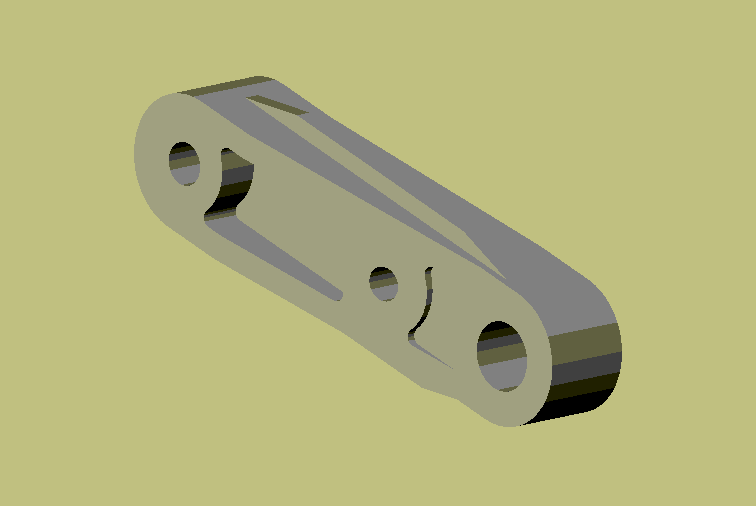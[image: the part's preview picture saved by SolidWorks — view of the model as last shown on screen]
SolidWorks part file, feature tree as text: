
SOLIDWORKS PART (.sldprt)
format: sldprt  version: not decoded by parser v0  size: 216,064 bytes
history: native  units: mm
features: sketch x9, cut_extrude x6, plane x4, extrude x3, material x1, fillet x1 (+8 scaffold rows collapsed)
feature tree (32):
  scaffold x8  (default folders/planes/origin — collapsed)
  material  "Matériau <non spécifié>"
  plane  "Plane1"
  plane  "Plane2"
  plane  "Plane3"
  sketch  "Esquisse1"  dims[c1.D1=8.0mm c1.D2=8.0mm c1.D3=25.0mm c2.D2=24.0mm]
  extrude  "Base-Extrusion"  Depth=9mm
  sketch  "Esquisse2"  dims[c1.D1=4.0mm c1.D2=4.0mm c1.D3=10.0mm c1.D4=3.0mm c1.D5=4.5mm c2.D1=5.0mm c2.D2=14.0mm c2.D3=4.0mm c2.D4=25.0mm c3.D1=12.5mm c3.D3=4.0mm c3.D4=4.0mm]
  extrude  "Boss.-Extru.1"  Depth=1mm
  sketch  "Esquisse3"  dims[D1=7.5mm]
  cut_extrude  "Enlèv. mat.-Extru.1"  [1 undecoded]
  sketch  "Esquisse4"  dims[D1=5.5mm D2=3.0mm D3=2.5mm]
  cut_extrude  "Enlèv. mat.-Extru.2"  [1 undecoded]
  sketch  "Esquisse5"  dims[c1.D1=3.0mm c1.D2=2.0mm c1.D4=3.0mm c2.D1=2.5mm c2.D3=16.0mm c3.D1=15.0mm c3.D3=15.0mm]
  cut_extrude  "Enlèv. mat.-Extru.3"  [1 undecoded]
  plane  "Plan1"  Offset=4mm
  sketch  "Esquisse11"  dims[D1=5.0mm]
  extrude  "Boss.-Extru.2"  Depth=0.5mm
  fillet  "Congé1"  Radius=0.5mm
  sketch  "Esquisse12"  dims[D1=2.5mm]
  cut_extrude  "Enlèv. mat.-Extru.5"  [1 undecoded]
  sketch  "Esquisse13"  dims[D1=4.0mm]
  cut_extrude  "Enlèv. mat.-Extru.6"  [1 undecoded]
  sketch  "Esquisse14"  dims[D3=6.0mm D4=6.0mm D5=6.0mm D7=0.5mm D1=9.0mm D2=24.0mm D6=5.0mm]
  cut_extrude  "Enlèv. mat.-Extru.7"  Depth=2.5mm
decode coverage: 14 of 19 modeling features carry decoded parameters
note: 5 parameter values undecoded
summary: no parameter record found for 5 features
note: suppression state not decoded; provenance and decode notes live in map.json
